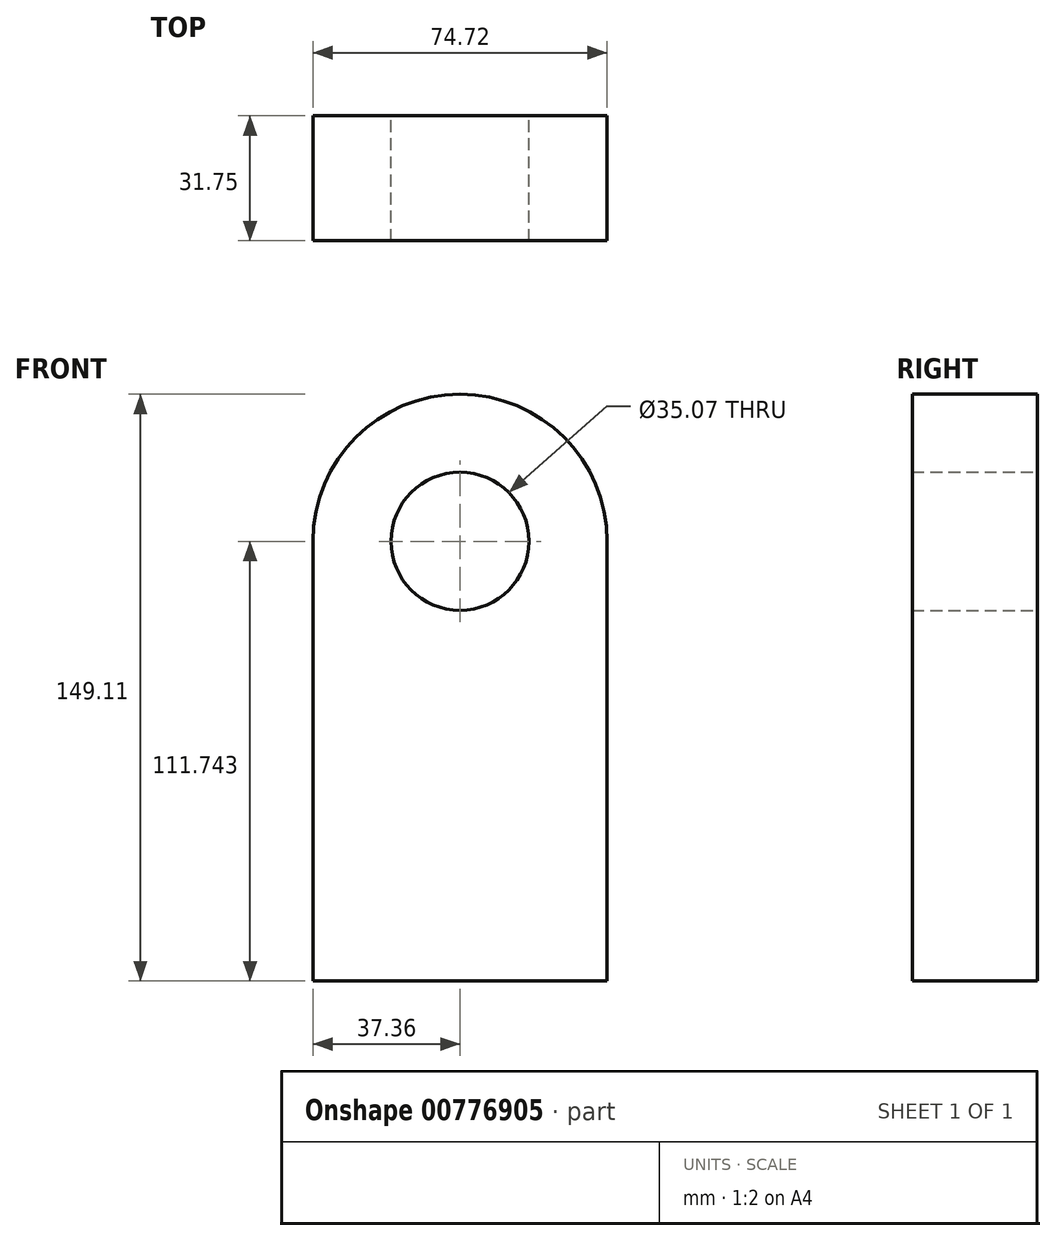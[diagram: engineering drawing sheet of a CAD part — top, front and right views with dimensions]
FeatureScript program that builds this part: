
annotation { "Feature Type Name" : "Feature", "Feature Type Description" : "" }
export const myFeature = defineFeature(function(context is Context, id is Id, definition is map)
    precondition{}
    {
        {
            var Q0;
            Q0=qCreatedBy(makeId("Front.planeOp"),FACE);
            var sketch = newSketch(context, id + "F0", { "sketchPlane" : qUnion([Q0])});
            skLineSegment(sketch, "E0.top", {"start": v(37.36, -55.87) * mm, "end": v(-37.36, -55.87) * mm});
            skLineSegment(sketch, "E0.left", {"start": v(37.36, 55.87) * mm, "end": v(37.36, -55.87) * mm});
            skLineSegment(sketch, "E0.right", {"start": v(-37.36, 55.87) * mm, "end": v(-37.36, -55.87) * mm});
            skPoint(sketch, "E0.middle", {"position": v(0, 0) * mm});
            skArc(sketch, "E1", {"start": v(37.36, 55.87) * mm, "mid": v(0, 93.24) * mm, "end": v(-37.36, 55.87) * mm});
            skCircle(sketch, "E2", {"center": v(0, 55.87) * mm, "radius": 17.53 * mm});
            skSolve(sketch);
        }
        {
            var Q0;
            Q0=makeQuery(id+"F0.imprint","IMPRINT",FACE,{"disambiguationData":[TD([[makeQuery(id+"F0.imprint","IMPRINT",EDGE,{"derivedFrom":sQuery(id+"F0.wireOp",EDGE,"E0.top")}),-1.0]])]});
            extrude(context, id + "F1", {"entities" : qUnion([Q0]), "depth" : 31.75 * mm, "offsetDistance" : 25.4 * mm});
        }
    });
